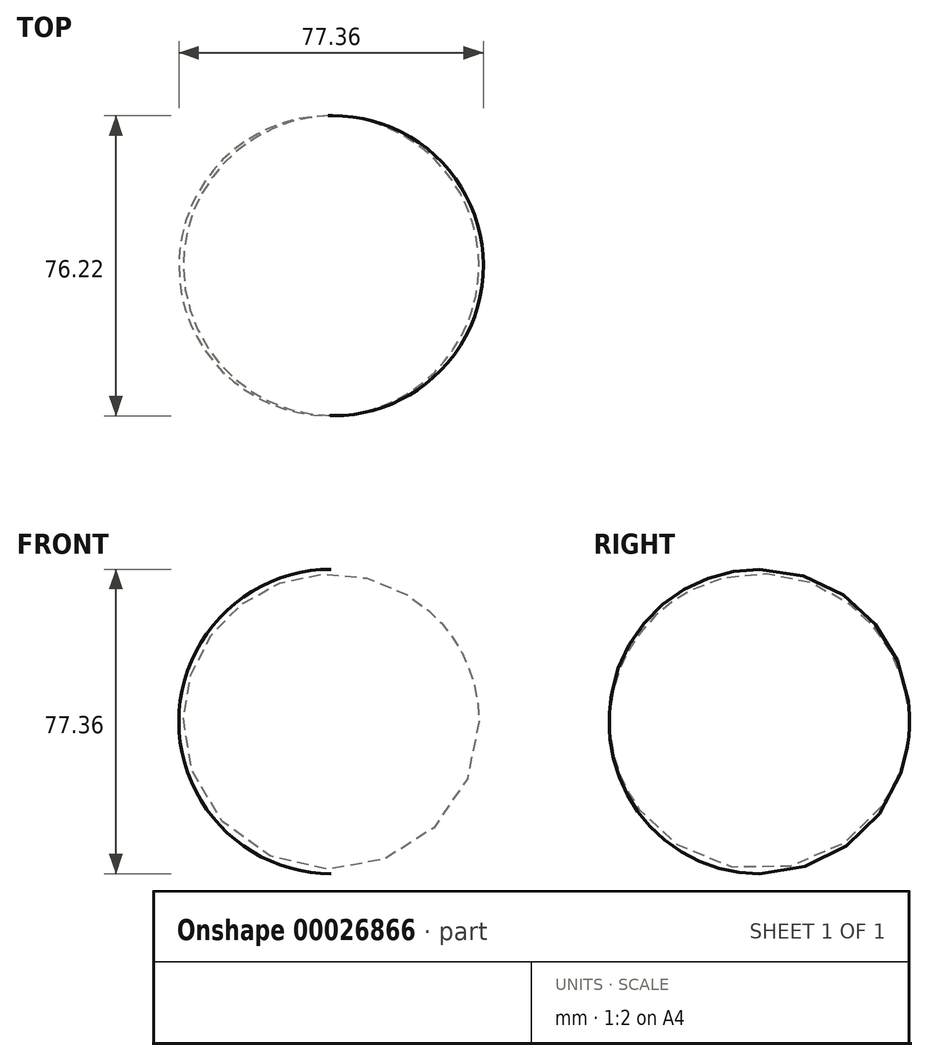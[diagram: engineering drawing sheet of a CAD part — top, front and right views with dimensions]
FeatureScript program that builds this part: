
annotation { "Feature Type Name" : "Feature", "Feature Type Description" : "" }
export const myFeature = defineFeature(function(context is Context, id is Id, definition is map)
    precondition{}
    {
        {
            var Q0;
            Q0=qCreatedBy(makeId("Top.planeOp"),FACE);
            var sketch = newSketch(context, id + "F0", { "sketchPlane" : qUnion([Q0])});
            skArc(sketch, "E0", {"start": v(-11.72, -29.26) * mm, "mid": v(26.7, 9.1) * mm, "end": v(-12.22, 46.94) * mm});
            skLineSegment(sketch, "E1", {"start": v(-12.22, 46.94) * mm, "end": v(-11.72, -29.26) * mm});
            skSolve(sketch);
        }
        {
            var Q0;
            Q0=makeQuery(id+"F0.imprint","IMPRINT",FACE,{"disambiguationData":[TD([[makeQuery(id+"F0.imprint","IMPRINT",EDGE,{"derivedFrom":sQuery(id+"F0.wireOp",EDGE,"E0")}),1.0]])]});
            var Q1;
            Q1=sQuery(id+"F0.wireOp",EDGE,"E1");
            revolve(context, id + "F1", {"entities" : qUnion([Q0]), "axis" : qUnion([Q1]), "revolveType" : RevolveType.FULL});
        }
    });
